# Revit family: Plumbing-Fix_Flush-Valve-Touchless_Stern_Venus
name_source: partatom
category: Plumbing Fixtures
units: mm (PartAtom-declared; Revit-internal decimal feet)

## family parameters
Classification Number = 23.45.05.14
Cut with Voids When Loaded = No
Enable Cutting in Views = No
Host = Face
Maintain Annotation Orientation = No
Part Type = Normal
Room Calculation Point = No
Round Connector Dimension = Use Diameter
Shared = No

## types (4) — shared parameters
Assembly Code = D2010300
Available Options = as Specified
Body Construction = Brass
CW Connection = Yes
CWFU = 1
Default Elevation = 0' - 0"
HW Connection = No
Manufacturer = Stern Engineering
Manufacturer Website = http://www.sternfaucets.com
Operating Pressure Range = 7.26 - 116 PSI  ;  0.5 - 8 bar
Operating Temperature Range = as Specified
Piping_Flow = 0 GPM
Piping_Inlet Diameter = 1"
Product Data = http://www.arcat.com
Product Features = 24 Hr Auto Flush
Revision = R1_2018-04
Sales Information = http://www.sternfaucets.com
Standards Conformance = as Specified
Type Comments = as Specified
URL = http://www.sternfaucets.com
Unit Height = 1' - 3 3/4"
Unit Width = 0' - 7 1/2"
Vent Connection = No
Warranty Duration (Years) = 2
Waste Connection = No
zero-valued in all types: Cost, Expected Lifespan (Years), HWFU, Maintenance Schedule (Months), WFU

## per-type parameters (varying)
| type | Description | GPF | Model | Power Supply |
| Battery Pack 1.28 GPF | Stern Touchless Flush Valve - Venus 1.28 GPF as Specified | 1.28 | Venus 1.28 GPF | 9V Battery |
| Battery Pack 1.6 GPF | Stern Touchless Flush Valve - Venus E 1.28 GPF as Specified | 1.6 | Venus E 1.28 GPF | 9V Battery |
| Transformer 1.28 GPF | Stern Touchless Flush Valve - Venus 3002 R as Specified | 1.28 | Venus 3002 R | 9V Transformer |
| Transformer 1.6 GPF | Stern Touchless Flush Valve - Venus 3002 RE as Specified | 1.6 | Venus 3002 RE | 9V Transformer |

## geometry (parser evidence)
native form markers: Sweep x1
no freeform markers — native parametric forms only
